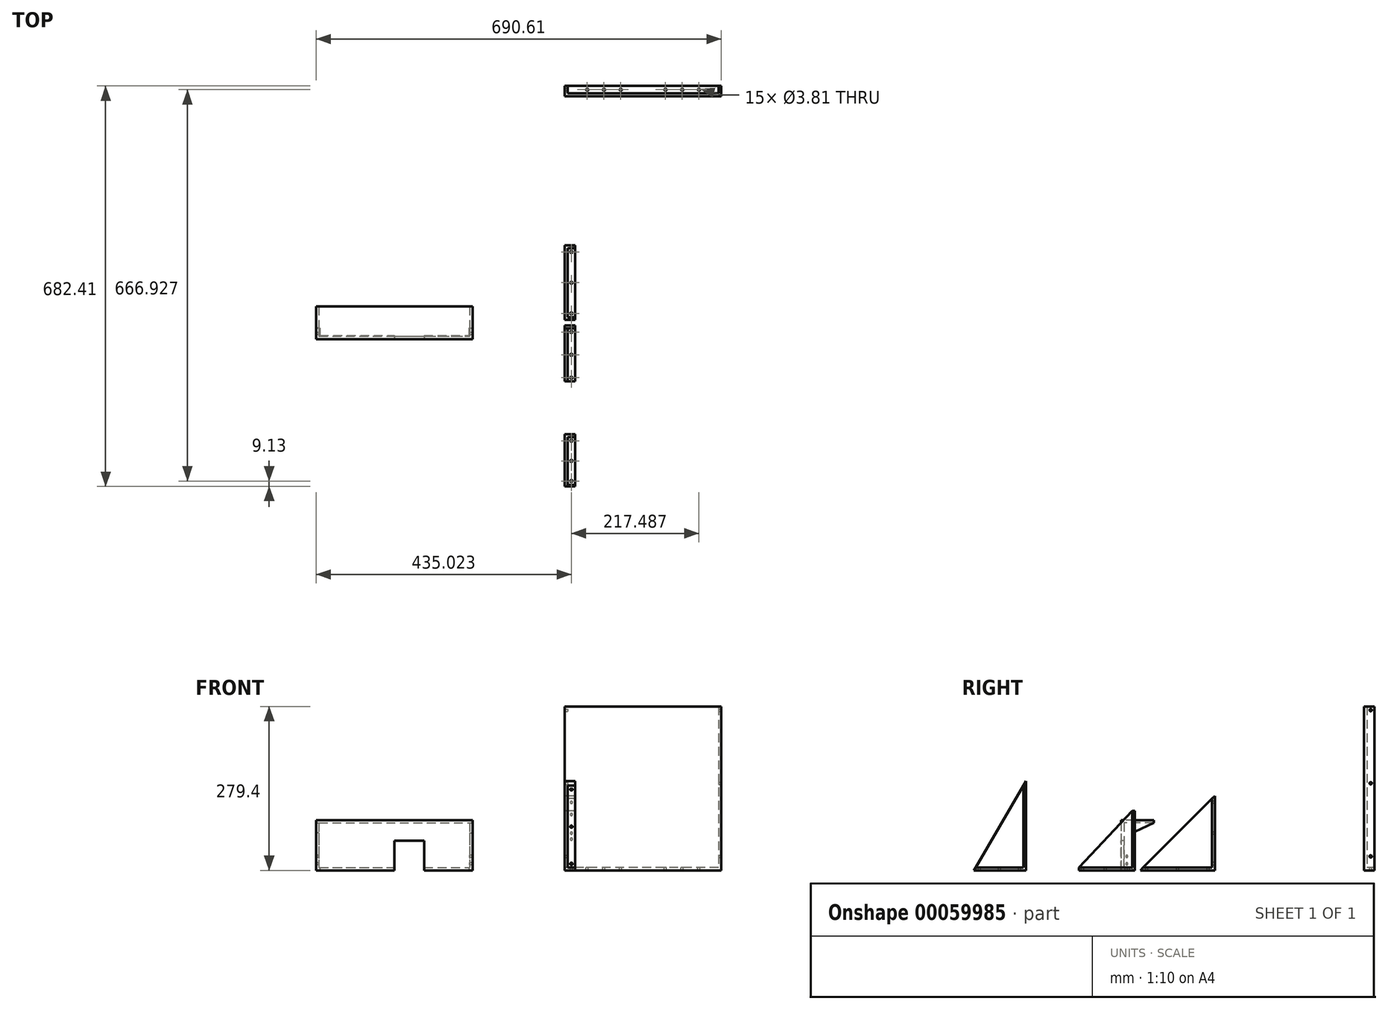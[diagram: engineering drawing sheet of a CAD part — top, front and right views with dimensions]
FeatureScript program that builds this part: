
annotation { "Feature Type Name" : "Feature", "Feature Type Description" : "" }
export const myFeature = defineFeature(function(context is Context, id is Id, definition is map)
    precondition{}
    {
        {
            var Q0;
            Q0=qCreatedBy(makeId("Right.planeOp"),FACE);
            var sketch = newSketch(context, id + "F0", { "sketchPlane" : qUnion([Q0])});
            skLineSegment(sketch, "E0", {"start": v(0, 0) * mm, "end": v(127, 127) * mm});
            skLineSegment(sketch, "E1", {"start": v(127, 127) * mm, "end": v(127, 0) * mm});
            skLineSegment(sketch, "E2", {"start": v(127, 0) * mm, "end": v(0, 0) * mm});
            skSolve(sketch);
        }
        {
            var Q0;
            Q0=makeQuery(id+"F0.imprint","IMPRINT",FACE,{"disambiguationData":[TD([[makeQuery(id+"F0.imprint","IMPRINT",EDGE,{"derivedFrom":sQuery(id+"F0.wireOp",EDGE,"E0")}),-1.0]])]});
            extrude(context, id + "F1", {"entities" : qUnion([Q0]), "depth" : 4.76 * mm});
        }
        {
            var Q0;
            Q0=makeQuery(id+"F1.opExtrude","CAP_FACE",FACE,{"disambiguationData":[OSD([sQuery(id+"F0.wireOp",EDGE,"E0"),sQuery(id+"F0.wireOp",EDGE,"E1"),sQuery(id+"F0.wireOp",EDGE,"E2")])],"isStart":false});
            var sketch = newSketch(context, id + "F2", { "sketchPlane" : qUnion([Q0])});
            skLineSegment(sketch, "E3", {"start": v(127, 4.76) * mm, "end": v(4.76, 4.76) * mm});
            skLineSegment(sketch, "E4", {"start": v(122.24, 4.76) * mm, "end": v(122.24, 122.24) * mm});
            skSolve(sketch);
        }
        {
            var Q0;
            {var subQ3=sQuery(id+"F2.wireOp",EDGE,"E4");Q0=makeQuery(id+"F2.imprint","IMPRINT",FACE,{"disambiguationData":[TD([[makeQuery(id+"F2.imprint","IMPRINT",EDGE,{"derivedFrom":subQ3}),-1.0]])]});}
            var Q1;
            {var subQ0=makeQuery(id+"F1.opExtrude","CAP_EDGE",EDGE,{"disambiguationData":[OSD([sQuery(id+"F0.wireOp",EDGE,"E2")])],"isStart":false});Q1=makeQuery(id+"F2.imprint","IMPRINT",FACE,{"disambiguationData":[TD([[makeQuery(id+"F2.imprint","IMPRINT",EDGE,{"derivedFrom":subQ0}),-1.0]])]});}
            extrude(context, id + "F3", {"entities" : qUnion([Q0, Q1]), "operationType" : NewBodyOperationType.ADD, "depth" : 12.7 * mm});
        }
        {
            var Q0;
            Q0=makeQuery(id+"F3.opExtrude","SWEPT_FACE",FACE,{"disambiguationData":[OSD([sQuery(id+"F2.wireOp",EDGE,"E3")])]});
            var sketch = newSketch(context, id + "F4", { "sketchPlane" : qUnion([Q0])});
            skCircle(sketch, "E5", {"center": v(11.11, 11.11) * mm, "radius": 1.9 * mm});
            skPoint(sketch, "E5.centerSnap0", {"position": v(11.11, 4.76) * mm});
            skCircle(sketch, "E6", {"center": v(11.11, 115.89) * mm, "radius": 1.9 * mm});
            skCircle(sketch, "E7", {"center": v(11.11, 63.5) * mm, "radius": 1.9 * mm});
            skPoint(sketch, "E7.centerSnap0", {"position": v(17.46, 63.5) * mm});
            skSolve(sketch);
        }
        {
            var Q0;
            Q0 = qSketchRegion(id + "F4", true);
            extrude(context, id + "F5", {"entities" : qUnion([Q0]), "operationType" : NewBodyOperationType.REMOVE, "endBound" : BoundingType.UP_TO_NEXT, "oppositeDirection" : true, "depth" : 25.4 * mm});
        }
        {
            var Q0;
            Q0=makeQuery(id+"F3.opExtrude","SWEPT_FACE",FACE,{"disambiguationData":[OSD([sQuery(id+"F2.wireOp",EDGE,"E4")])]});
            var sketch = newSketch(context, id + "F6", { "sketchPlane" : qUnion([Q0])});
            skCircle(sketch, "E8", {"center": v(11.11, 115.89) * mm, "radius": 1.9 * mm});
            skPoint(sketch, "E8.centerSnap0", {"position": v(11.11, 122.24) * mm});
            skCircle(sketch, "E9", {"center": v(11.11, 11.11) * mm, "radius": 2.54 * mm});
            skCircle(sketch, "E10", {"center": v(11.11, 63.5) * mm, "radius": 1.9 * mm});
            skPoint(sketch, "E10.centerSnap0", {"position": v(17.46, 63.5) * mm});
            skSolve(sketch);
        }
        {
            var Q0;
            Q0=makeQuery(id+"F6.imprint","IMPRINT",FACE,{"disambiguationData":[TD([[makeQuery(id+"F6.imprint","IMPRINT",EDGE,{"derivedFrom":sQuery(id+"F6.wireOp",EDGE,"E8")}),1.0]])]});
            var Q1;
            Q1=makeQuery(id+"F6.imprint","IMPRINT",FACE,{"disambiguationData":[TD([[makeQuery(id+"F6.imprint","IMPRINT",EDGE,{"derivedFrom":sQuery(id+"F6.wireOp",EDGE,"E9")}),1.0]])]});
            var Q2;
            Q2=makeQuery(id+"F6.imprint","IMPRINT",FACE,{"disambiguationData":[TD([[makeQuery(id+"F6.imprint","IMPRINT",EDGE,{"derivedFrom":sQuery(id+"F6.wireOp",EDGE,"E10")}),1.0]])]});
            extrude(context, id + "F7", {"entities" : qUnion([Q0, Q1, Q2]), "operationType" : NewBodyOperationType.REMOVE, "endBound" : BoundingType.UP_TO_NEXT, "oppositeDirection" : true, "depth" : 25.4 * mm});
        }
        {
            var Q0;
            Q0=qCreatedBy(makeId("Right.planeOp"),FACE);
            var sketch = newSketch(context, id + "F8", { "sketchPlane" : qUnion([Q0])});
            skLineSegment(sketch, "E11", {"start": v(-283.58, 0) * mm, "end": v(-194.68, 152.4) * mm});
            skLineSegment(sketch, "E12", {"start": v(-194.68, 152.4) * mm, "end": v(-194.68, 0) * mm});
            skLineSegment(sketch, "E13", {"start": v(-194.68, 0) * mm, "end": v(-283.58, 0) * mm});
            skSolve(sketch);
        }
        {
            var Q0;
            Q0=makeQuery(id+"F8.imprint","IMPRINT",FACE,{"disambiguationData":[TD([[makeQuery(id+"F8.imprint","IMPRINT",EDGE,{"derivedFrom":sQuery(id+"F8.wireOp",EDGE,"E11")}),-1.0]])]});
            extrude(context, id + "F9", {"entities" : qUnion([Q0]), "depth" : 4.76 * mm});
        }
        {
            var Q0;
            Q0=makeQuery(id+"F9.opExtrude","CAP_FACE",FACE,{"disambiguationData":[OSD([sQuery(id+"F8.wireOp",EDGE,"E11"),sQuery(id+"F8.wireOp",EDGE,"E12"),sQuery(id+"F8.wireOp",EDGE,"E13")])],"isStart":false});
            var sketch = newSketch(context, id + "F10", { "sketchPlane" : qUnion([Q0])});
            skLineSegment(sketch, "E14", {"start": v(-280.8, 4.76) * mm, "end": v(-194.68, 4.76) * mm});
            skLineSegment(sketch, "E15", {"start": v(-199.44, 4.76) * mm, "end": v(-199.44, 144.24) * mm});
            skSolve(sketch);
        }
        {
            var Q0;
            {var subQ3=sQuery(id+"F10.wireOp",EDGE,"E15");Q0=makeQuery(id+"F10.imprint","IMPRINT",FACE,{"disambiguationData":[TD([[makeQuery(id+"F10.imprint","IMPRINT",EDGE,{"derivedFrom":subQ3}),-1.0]])]});}
            var Q1;
            {var subQ0=makeQuery(id+"F9.opExtrude","CAP_EDGE",EDGE,{"disambiguationData":[OSD([sQuery(id+"F8.wireOp",EDGE,"E13")])],"isStart":false});Q1=makeQuery(id+"F10.imprint","IMPRINT",FACE,{"disambiguationData":[TD([[makeQuery(id+"F10.imprint","IMPRINT",EDGE,{"derivedFrom":subQ0}),-1.0]])]});}
            extrude(context, id + "F11", {"entities" : qUnion([Q0, Q1]), "operationType" : NewBodyOperationType.ADD, "depth" : 12.7 * mm});
        }
        {
            var Q0;
            Q0=makeQuery(id+"F11.opExtrude","SWEPT_FACE",FACE,{"disambiguationData":[OSD([sQuery(id+"F10.wireOp",EDGE,"E14")])]});
            var sketch = newSketch(context, id + "F12", { "sketchPlane" : qUnion([Q0])});
            skCircle(sketch, "E16", {"center": v(11.11, -274.45) * mm, "radius": 1.9 * mm});
            skPoint(sketch, "E16.centerSnap0", {"position": v(11.11, -280.8) * mm});
            skCircle(sketch, "E17", {"center": v(11.11, -205.8) * mm, "radius": 1.9 * mm});
            skPoint(sketch, "E17.centerSnap0", {"position": v(11.11, -199.44) * mm});
            skCircle(sketch, "E18", {"center": v(11.11, -240.12) * mm, "radius": 1.9 * mm});
            skPoint(sketch, "E18.centerSnap0", {"position": v(17.46, -240.12) * mm});
            skSolve(sketch);
        }
        {
            var Q0;
            Q0=makeQuery(id+"F12.imprint","IMPRINT",FACE,{"disambiguationData":[TD([[makeQuery(id+"F12.imprint","IMPRINT",EDGE,{"derivedFrom":sQuery(id+"F12.wireOp",EDGE,"E16")}),1.0]])]});
            var Q1;
            Q1=makeQuery(id+"F12.imprint","IMPRINT",FACE,{"disambiguationData":[TD([[makeQuery(id+"F12.imprint","IMPRINT",EDGE,{"derivedFrom":sQuery(id+"F12.wireOp",EDGE,"E18")}),1.0]])]});
            var Q2;
            Q2=makeQuery(id+"F12.imprint","IMPRINT",FACE,{"disambiguationData":[TD([[makeQuery(id+"F12.imprint","IMPRINT",EDGE,{"derivedFrom":sQuery(id+"F12.wireOp",EDGE,"E17")}),1.0]])]});
            extrude(context, id + "F13", {"entities" : qUnion([Q0, Q1, Q2]), "operationType" : NewBodyOperationType.REMOVE, "endBound" : BoundingType.UP_TO_NEXT, "oppositeDirection" : true, "depth" : 25.4 * mm});
        }
        {
            var Q0;
            Q0=makeQuery(id+"F11.opExtrude","SWEPT_FACE",FACE,{"disambiguationData":[OSD([sQuery(id+"F10.wireOp",EDGE,"E15")])]});
            var sketch = newSketch(context, id + "F14", { "sketchPlane" : qUnion([Q0])});
            skCircle(sketch, "E19", {"center": v(11.11, 137.89) * mm, "radius": 1.9 * mm});
            skPoint(sketch, "E19.centerSnap0", {"position": v(11.11, 144.24) * mm});
            skCircle(sketch, "E20", {"center": v(11.11, 11.11) * mm, "radius": 1.9 * mm});
            skPoint(sketch, "E20.centerSnap0", {"position": v(11.11, 4.76) * mm});
            skCircle(sketch, "E21", {"center": v(11.11, 74.5) * mm, "radius": 1.9 * mm});
            skPoint(sketch, "E21.centerSnap0", {"position": v(4.76, 74.5) * mm});
            skSolve(sketch);
        }
        {
            var Q0;
            Q0 = qSketchRegion(id + "F14", true);
            extrude(context, id + "F15", {"entities" : qUnion([Q0]), "operationType" : NewBodyOperationType.REMOVE, "endBound" : BoundingType.UP_TO_NEXT, "oppositeDirection" : true, "depth" : 25.4 * mm});
        }
        {
            var Q0;
            Q0=qCreatedBy(makeId("Right.planeOp"),FACE);
            var sketch = newSketch(context, id + "F16", { "sketchPlane" : qUnion([Q0])});
            skLineSegment(sketch, "E22", {"start": v(-104.62, 0) * mm, "end": v(-9.37, 0) * mm});
            skLineSegment(sketch, "E23", {"start": v(-9.37, 0) * mm, "end": v(-9.37, 101.6) * mm});
            skLineSegment(sketch, "E24", {"start": v(-9.37, 101.6) * mm, "end": v(-14.14, 101.6) * mm});
            skLineSegment(sketch, "E25", {"start": v(-14.14, 101.6) * mm, "end": v(-104.62, 4.76) * mm});
            skLineSegment(sketch, "E26", {"start": v(-104.62, 4.76) * mm, "end": v(-104.62, 0) * mm});
            skLineSegment(sketch, "E27", {"start": v(-104.62, 4.76) * mm, "end": v(-14.14, 4.76) * mm});
            skLineSegment(sketch, "E28", {"start": v(-14.14, 4.76) * mm, "end": v(-14.14, 101.6) * mm});
            skSolve(sketch);
        }
        {
            var Q0;
            Q0 = qSketchRegion(id + "F16", true);
            extrude(context, id + "F17", {"entities" : qUnion([Q0]), "depth" : 4.76 * mm});
        }
        {
            var Q0;
            Q0=makeQuery(id+"F17.opExtrude","CAP_FACE",FACE,{"disambiguationData":[OSD([sQuery(id+"F16.wireOp",EDGE,"E22"),sQuery(id+"F16.wireOp",EDGE,"E23"),sQuery(id+"F16.wireOp",EDGE,"E24"),sQuery(id+"F16.wireOp",EDGE,"E25"),sQuery(id+"F16.wireOp",EDGE,"E26")])],"isStart":false});
            var sketch = newSketch(context, id + "F18", { "sketchPlane" : qUnion([Q0])});
            skLineSegment(sketch, "E29", {"start": v(-14.14, 101.6) * mm, "end": v(-14.14, 4.76) * mm});
            skLineSegment(sketch, "E30", {"start": v(-14.14, 4.76) * mm, "end": v(-104.62, 4.76) * mm});
            skSolve(sketch);
        }
        {
            var Q0;
            Q0=makeQuery(id+"F18.imprint","IMPRINT",FACE,{"disambiguationData":[TD([[makeQuery(id+"F18.imprint","IMPRINT",EDGE,{"derivedFrom":sQuery(id+"F18.wireOp",EDGE,"E29")}),1.0]])]});
            extrude(context, id + "F19", {"entities" : qUnion([Q0]), "operationType" : NewBodyOperationType.ADD, "depth" : 12.7 * mm});
        }
        {
            var Q0;
            Q0=makeQuery(id+"F19.opExtrude","SWEPT_FACE",FACE,{"disambiguationData":[OSD([sQuery(id+"F18.wireOp",EDGE,"E30")])]});
            var sketch = newSketch(context, id + "F20", { "sketchPlane" : qUnion([Q0])});
            skCircle(sketch, "E31", {"center": v(11.11, -98.27) * mm, "radius": 1.9 * mm});
            skPoint(sketch, "E31.centerSnap0", {"position": v(11.11, -104.62) * mm});
            skCircle(sketch, "E32", {"center": v(11.11, -20.49) * mm, "radius": 1.9 * mm});
            skPoint(sketch, "E32.centerSnap0", {"position": v(11.11, -14.14) * mm});
            skCircle(sketch, "E33", {"center": v(11.11, -59.38) * mm, "radius": 1.9 * mm});
            skPoint(sketch, "E33.centerSnap0", {"position": v(17.46, -59.38) * mm});
            skSolve(sketch);
        }
        {
            var Q0;
            Q0 = qSketchRegion(id + "F20", true);
            extrude(context, id + "F21", {"entities" : qUnion([Q0]), "operationType" : NewBodyOperationType.REMOVE, "endBound" : BoundingType.UP_TO_NEXT, "oppositeDirection" : true, "depth" : 25.4 * mm});
        }
        {
            var Q0;
            Q0=makeQuery(id+"F19.opExtrude","SWEPT_FACE",FACE,{"disambiguationData":[OSD([sQuery(id+"F18.wireOp",EDGE,"E29")])]});
            var sketch = newSketch(context, id + "F22", { "sketchPlane" : qUnion([Q0])});
            skCircle(sketch, "E34", {"center": v(11.11, 95.25) * mm, "radius": 1.9 * mm});
            skPoint(sketch, "E34.centerSnap0", {"position": v(11.11, 101.6) * mm});
            skCircle(sketch, "E35", {"center": v(11.11, 11.11) * mm, "radius": 1.9 * mm});
            skPoint(sketch, "E35.centerSnap0", {"position": v(11.11, 4.76) * mm});
            skCircle(sketch, "E36", {"center": v(11.11, 53.18) * mm, "radius": 1.9 * mm});
            skPoint(sketch, "E36.centerSnap0", {"position": v(17.46, 53.18) * mm});
            skSolve(sketch);
        }
        {
            var Q0;
            Q0 = qSketchRegion(id + "F22", true);
            extrude(context, id + "F23", {"entities" : qUnion([Q0]), "operationType" : NewBodyOperationType.REMOVE, "endBound" : BoundingType.UP_TO_NEXT, "oppositeDirection" : true, "depth" : 25.4 * mm});
        }
        {
            var Q0;
            Q0=qCreatedBy(makeId("Top.planeOp"),FACE);
            var sketch = newSketch(context, id + "F24", { "sketchPlane" : qUnion([Q0])});
            skLineSegment(sketch, "E37.bottom", {"start": v(-423.91, -13.53) * mm, "end": v(-157.21, -13.53) * mm});
            skLineSegment(sketch, "E37.top", {"start": v(-423.91, -32.58) * mm, "end": v(-157.21, -32.58) * mm});
            skLineSegment(sketch, "E37.left", {"start": v(-423.91, -13.53) * mm, "end": v(-423.91, -32.58) * mm});
            skLineSegment(sketch, "E37.right", {"start": v(-157.21, -13.53) * mm, "end": v(-157.21, -32.58) * mm});
            skLineSegment(sketch, "E38.bottom", {"start": v(-417.56, -13.53) * mm, "end": v(-163.56, -13.53) * mm});
            skLineSegment(sketch, "E38.top", {"start": v(-417.56, -26.23) * mm, "end": v(-163.56, -26.23) * mm});
            skLineSegment(sketch, "E38.left", {"start": v(-417.56, -13.53) * mm, "end": v(-417.56, -26.23) * mm});
            skLineSegment(sketch, "E38.right", {"start": v(-163.56, -13.53) * mm, "end": v(-163.56, -26.23) * mm});
            skSolve(sketch);
        }
        {
            var Q0;
            Q0=makeQuery(id+"F24.imprint","IMPRINT",FACE,{"disambiguationData":[TD([[makeQuery(id+"F24.imprint","IMPRINT",EDGE,{"derivedFrom":sQuery(id+"F24.wireOp",EDGE,"E38.bottom")}),-1.0]])]});
            var Q1;
            Q1=makeQuery(id+"F24.imprint","IMPRINT",FACE,{"disambiguationData":[TD([[makeQuery(id+"F24.imprint","IMPRINT",EDGE,{"derivedFrom":sQuery(id+"F24.wireOp",EDGE,"E37.top")}),1.0]])]});
            extrude(context, id + "F25", {"entities" : qUnion([Q0, Q1]), "depth" : 4.76 * mm});
        }
        {
            var Q0;
            Q0=makeQuery(id+"F25.opExtrude","CAP_FACE",FACE,{"disambiguationData":[OSD([sQuery(id+"F24.wireOp",EDGE,"E37.bottom"),sQuery(id+"F24.wireOp",EDGE,"E37.top"),sQuery(id+"F24.wireOp",EDGE,"E37.left"),sQuery(id+"F24.wireOp",EDGE,"E37.right"),sQuery(id+"F24.wireOp",EDGE,"E38.bottom")])],"isStart":false});
            var sketch = newSketch(context, id + "F26", { "sketchPlane" : qUnion([Q0])});
            skLineSegment(sketch, "E39.bottom", {"start": v(-419.15, -13.53) * mm, "end": v(-161.97, -13.53) * mm});
            skLineSegment(sketch, "E39.top", {"start": v(-419.15, -27.82) * mm, "end": v(-161.97, -27.82) * mm});
            skLineSegment(sketch, "E39.left", {"start": v(-419.15, -13.53) * mm, "end": v(-419.15, -27.82) * mm});
            skLineSegment(sketch, "E39.right", {"start": v(-161.97, -13.53) * mm, "end": v(-161.97, -27.82) * mm});
            skSolve(sketch);
        }
        {
            var Q0;
            Q0=makeQuery(id+"F26.imprint","IMPRINT",FACE,{"disambiguationData":[TD([[makeQuery(id+"F26.imprint","IMPRINT",EDGE,{"derivedFrom":sQuery(id+"F26.wireOp",EDGE,"E39.top")}),-1.0]])]});
            extrude(context, id + "F27", {"entities" : qUnion([Q0]), "operationType" : NewBodyOperationType.ADD, "depth" : 76.2 * mm});
        }
        {
            var Q0;
            {var subQ0=sQuery(id+"F24.wireOp",EDGE,"E37.left");Q0=makeQuery(id+"F27.boolean.opBoolean","MERGE",FACE,{"derivedFrom":[makeQuery(id+"F25.opExtrude","SWEPT_FACE",FACE,{"disambiguationData":[OSD([subQ0])]}),makeQuery(id+"F27.opExtrude","SWEPT_FACE",FACE,{"disambiguationData":[OSD([subQ0])]})]});}
            var sketch = newSketch(context, id + "F28", { "sketchPlane" : qUnion([Q0])});
            skCircle(sketch, "E40", {"center": v(23.06, 11.11) * mm, "radius": 1.9 * mm});
            skCircle(sketch, "E41", {"center": v(23.06, 23.81) * mm, "radius": 1.9 * mm});
            skSolve(sketch);
        }
        {
            var Q0;
            Q0=makeQuery(id+"F28.imprint","IMPRINT",FACE,{"disambiguationData":[TD([[makeQuery(id+"F28.imprint","IMPRINT",EDGE,{"derivedFrom":sQuery(id+"F28.wireOp",EDGE,"E41")}),1.0]])]});
            var Q1;
            Q1=makeQuery(id+"F28.imprint","IMPRINT",FACE,{"disambiguationData":[TD([[makeQuery(id+"F28.imprint","IMPRINT",EDGE,{"derivedFrom":sQuery(id+"F28.wireOp",EDGE,"E40")}),1.0]])]});
            var Q2;
            {var subQ0=sQuery(id+"F24.wireOp",EDGE,"E37.right");Q2=makeQuery(id+"F27.boolean.opBoolean","MERGE",FACE,{"derivedFrom":[makeQuery(id+"F25.opExtrude","SWEPT_FACE",FACE,{"disambiguationData":[OSD([subQ0])]}),makeQuery(id+"F27.opExtrude","SWEPT_FACE",FACE,{"disambiguationData":[OSD([subQ0])]})]});}
            extrude(context, id + "F29", {"entities" : qUnion([Q0, Q1]), "operationType" : NewBodyOperationType.REMOVE, "endBound" : BoundingType.UP_TO_SURFACE, "oppositeDirection" : true, "endBoundEntityFace" : qUnion([Q2]), "depth" : 25.4 * mm});
        }
        {
            var Q0;
            {var subQ0=sQuery(id+"F24.wireOp",EDGE,"E37.top");Q0=makeQuery(id+"F27.boolean.opBoolean","MERGE",FACE,{"derivedFrom":[makeQuery(id+"F25.opExtrude","SWEPT_FACE",FACE,{"disambiguationData":[OSD([subQ0])]}),makeQuery(id+"F27.opExtrude","SWEPT_FACE",FACE,{"disambiguationData":[OSD([subQ0])]})]});}
            var sketch = newSketch(context, id + "F30", { "sketchPlane" : qUnion([Q0])});
            skLineSegment(sketch, "E42.bottom", {"start": v(-290.56, 0) * mm, "end": v(-239.76, 0) * mm});
            skLineSegment(sketch, "E42.top", {"start": v(-290.56, 50.8) * mm, "end": v(-239.76, 50.8) * mm});
            skLineSegment(sketch, "E42.left", {"start": v(-290.56, 0) * mm, "end": v(-290.56, 50.8) * mm});
            skLineSegment(sketch, "E42.right", {"start": v(-239.76, 0) * mm, "end": v(-239.76, 50.8) * mm});
            skLineSegment(sketch, "E43", {"start": v(-290.56, 50.8) * mm, "end": v(-423.91, 50.8) * mm, "construction": true});
            skLineSegment(sketch, "E44", {"start": v(-239.76, 50.8) * mm, "end": v(-157.21, 50.8) * mm, "construction": true});
            skSolve(sketch);
        }
        {
            var Q0;
            Q0=makeQuery(id+"F30.imprint","IMPRINT",FACE,{"disambiguationData":[TD([[makeQuery(id+"F30.imprint","IMPRINT",EDGE,{"derivedFrom":sQuery(id+"F30.wireOp",EDGE,"E42.bottom")}),1.0]])]});
            extrude(context, id + "F31", {"entities" : qUnion([Q0]), "operationType" : NewBodyOperationType.REMOVE, "endBound" : BoundingType.UP_TO_NEXT, "oppositeDirection" : true, "depth" : 25.4 * mm});
        }
        {
            var Q0;
            Q0=makeQuery(id+"F27.opExtrude","CAP_FACE",FACE,{"disambiguationData":[OSD([sQuery(id+"F24.wireOp",EDGE,"E37.bottom"),sQuery(id+"F24.wireOp",EDGE,"E37.top"),sQuery(id+"F24.wireOp",EDGE,"E37.left"),sQuery(id+"F24.wireOp",EDGE,"E37.right"),sQuery(id+"F24.wireOp",EDGE,"E38.bottom"),sQuery(id+"F26.wireOp",EDGE,"E39.top"),sQuery(id+"F26.wireOp",EDGE,"E39.left"),sQuery(id+"F26.wireOp",EDGE,"E39.right")])],"isStart":false});
            var sketch = newSketch(context, id + "F32", { "sketchPlane" : qUnion([Q0])});
            skLineSegment(sketch, "E45.bottom", {"start": v(-423.91, -32.58) * mm, "end": v(-157.21, -32.58) * mm});
            skLineSegment(sketch, "E45.top", {"start": v(-423.91, -27.82) * mm, "end": v(-157.21, -27.82) * mm});
            skLineSegment(sketch, "E45.left", {"start": v(-423.91, -32.58) * mm, "end": v(-423.91, -27.82) * mm});
            skLineSegment(sketch, "E45.right", {"start": v(-157.21, -32.58) * mm, "end": v(-157.21, -27.82) * mm});
            skSolve(sketch);
        }
        {
            var Q0;
            Q0=makeQuery(id+"F32.imprint","IMPRINT",FACE,{"disambiguationData":[TD([[makeQuery(id+"F32.imprint","IMPRINT",EDGE,{"derivedFrom":sQuery(id+"F32.wireOp",EDGE,"E45.bottom")}),1.0]])]});
            extrude(context, id + "F33", {"entities" : qUnion([Q0]), "operationType" : NewBodyOperationType.ADD, "depth" : 4.76 * mm});
        }
        {
            var Q0;
            Q0=makeQuery(id+"F33.boolean.opBoolean","MERGE",FACE,{"derivedFrom":[makeQuery(id+"F27.opExtrude","SWEPT_FACE",FACE,{"disambiguationData":[OSD([sQuery(id+"F26.wireOp",EDGE,"E39.top")])]}),makeQuery(id+"F33.opExtrude","SWEPT_FACE",FACE,{"disambiguationData":[OSD([sQuery(id+"F32.wireOp",EDGE,"E45.top")])]})]});
            var sketch = newSketch(context, id + "F34", { "sketchPlane" : qUnion([Q0])});
            skLineSegment(sketch, "E46.bottom", {"start": v(157.21, 85.73) * mm, "end": v(423.91, 85.73) * mm});
            skLineSegment(sketch, "E46.top", {"start": v(157.21, 80.96) * mm, "end": v(423.91, 80.96) * mm});
            skLineSegment(sketch, "E46.left", {"start": v(157.21, 85.73) * mm, "end": v(157.21, 80.96) * mm});
            skLineSegment(sketch, "E46.right", {"start": v(423.91, 85.73) * mm, "end": v(423.91, 80.96) * mm});
            skSolve(sketch);
        }
        {
            var Q0;
            Q0=makeQuery(id+"F34.imprint","IMPRINT",FACE,{"disambiguationData":[TD([[makeQuery(id+"F34.imprint","IMPRINT",EDGE,{"derivedFrom":sQuery(id+"F34.wireOp",EDGE,"E46.bottom")}),1.0]])]});
            extrude(context, id + "F35", {"entities" : qUnion([Q0]), "operationType" : NewBodyOperationType.ADD, "depth" : 50.8 * mm});
        }
        {
            var Q0;
            {var subQ0=sQuery(id+"F24.wireOp",EDGE,"E37.left");Q0=makeQuery(id+"F35.boolean.opBoolean","MERGE",FACE,{"derivedFrom":[makeQuery(id+"F33.boolean.opBoolean","MERGE",FACE,{"derivedFrom":[makeQuery(id+"F27.boolean.opBoolean","MERGE",FACE,{"derivedFrom":[makeQuery(id+"F25.opExtrude","SWEPT_FACE",FACE,{"disambiguationData":[OSD([subQ0])]}),makeQuery(id+"F27.opExtrude","SWEPT_FACE",FACE,{"disambiguationData":[OSD([subQ0])]})]}),makeQuery(id+"F33.opExtrude","SWEPT_FACE",FACE,{"disambiguationData":[OSD([sQuery(id+"F32.wireOp",EDGE,"E45.left")])]})]}),makeQuery(id+"F35.opExtrude","SWEPT_FACE",FACE,{"disambiguationData":[OSD([sQuery(id+"F34.wireOp",EDGE,"E46.right")])]})]});}
            var sketch = newSketch(context, id + "F36", { "sketchPlane" : qUnion([Q0])});
            skLineSegment(sketch, "E47", {"start": v(-22.98, 80.96) * mm, "end": v(13.53, 63.94) * mm});
            skSolve(sketch);
        }
        {
            var Q0;
            {var subQ0=sQuery(id+"F36.wireOp",EDGE,"E47");Q0=makeQuery(id+"F36.imprint","IMPRINT",FACE,{"disambiguationData":[TD([[makeQuery(id+"F36.imprint","IMPRINT",EDGE,{"derivedFrom":subQ0}),1.0]])]});}
            extrude(context, id + "F37", {"entities" : qUnion([Q0]), "operationType" : NewBodyOperationType.ADD, "oppositeDirection" : true, "depth" : 4.76 * mm});
        }
        {
            var Q0;
            {var subQ0=sQuery(id+"F24.wireOp",EDGE,"E37.right");Q0=makeQuery(id+"F35.boolean.opBoolean","MERGE",FACE,{"derivedFrom":[makeQuery(id+"F33.boolean.opBoolean","MERGE",FACE,{"derivedFrom":[makeQuery(id+"F27.boolean.opBoolean","MERGE",FACE,{"derivedFrom":[makeQuery(id+"F25.opExtrude","SWEPT_FACE",FACE,{"disambiguationData":[OSD([subQ0])]}),makeQuery(id+"F27.opExtrude","SWEPT_FACE",FACE,{"disambiguationData":[OSD([subQ0])]})]}),makeQuery(id+"F33.opExtrude","SWEPT_FACE",FACE,{"disambiguationData":[OSD([sQuery(id+"F32.wireOp",EDGE,"E45.right")])]})]}),makeQuery(id+"F35.opExtrude","SWEPT_FACE",FACE,{"disambiguationData":[OSD([sQuery(id+"F34.wireOp",EDGE,"E46.left")])]})]});}
            var sketch = newSketch(context, id + "F38", { "sketchPlane" : qUnion([Q0])});
            skLineSegment(sketch, "E48", {"start": v(22.98, 80.96) * mm, "end": v(-13.53, 63.94) * mm});
            skSolve(sketch);
        }
        {
            var Q0;
            {var subQ0=sQuery(id+"F38.wireOp",EDGE,"E48");Q0=makeQuery(id+"F38.imprint","IMPRINT",FACE,{"disambiguationData":[TD([[makeQuery(id+"F38.imprint","IMPRINT",EDGE,{"derivedFrom":subQ0}),-1.0]])]});}
            extrude(context, id + "F39", {"entities" : qUnion([Q0]), "operationType" : NewBodyOperationType.ADD, "oppositeDirection" : true, "depth" : 4.76 * mm});
        }
        {
            var Q0;
            Q0=qCreatedBy(makeId("Right.planeOp"),FACE);
            var sketch = newSketch(context, id + "F40", { "sketchPlane" : qUnion([Q0])});
            skLineSegment(sketch, "E49.bottom", {"start": v(381.37, 0) * mm, "end": v(386.13, 0) * mm});
            skLineSegment(sketch, "E49.top", {"start": v(381.37, 279.4) * mm, "end": v(386.13, 279.4) * mm});
            skLineSegment(sketch, "E49.left", {"start": v(381.37, 0) * mm, "end": v(381.37, 279.4) * mm});
            skLineSegment(sketch, "E49.right", {"start": v(386.13, 0) * mm, "end": v(386.13, 279.4) * mm});
            skSolve(sketch);
        }
        {
            var Q0;
            Q0=makeQuery(id+"F40.imprint","IMPRINT",FACE,{"disambiguationData":[TD([[makeQuery(id+"F40.imprint","IMPRINT",EDGE,{"derivedFrom":sQuery(id+"F40.wireOp",EDGE,"E49.bottom")}),1.0]])]});
            extrude(context, id + "F41", {"entities" : qUnion([Q0]), "depth" : 266.7 * mm});
        }
        {
            var Q0;
            Q0=makeQuery(id+"F41.opExtrude","SWEPT_FACE",FACE,{"disambiguationData":[OSD([sQuery(id+"F40.wireOp",EDGE,"E49.right")])]});
            var sketch = newSketch(context, id + "F42", { "sketchPlane" : qUnion([Q0])});
            skLineSegment(sketch, "E50", {"start": v(-133.35, 279.4) * mm, "end": v(-133.35, 0) * mm, "construction": true});
            skLineSegment(sketch, "E51.bottom", {"start": v(-266.7, 279.4) * mm, "end": v(-261.94, 279.4) * mm});
            skLineSegment(sketch, "E51.top", {"start": v(-266.7, 0) * mm, "end": v(-261.94, 0) * mm});
            skLineSegment(sketch, "E51.left", {"start": v(-266.7, 279.4) * mm, "end": v(-266.7, 0) * mm});
            skLineSegment(sketch, "E51.right", {"start": v(-261.94, 279.4) * mm, "end": v(-261.94, 0) * mm});
            skLineSegment(sketch, "E52.bottom", {"start": v(-261.94, 0) * mm, "end": v(-133.35, 0) * mm});
            skLineSegment(sketch, "E52.top", {"start": v(-261.94, 4.76) * mm, "end": v(-133.35, 4.76) * mm});
            skLineSegment(sketch, "E52.left", {"start": v(-261.94, 0) * mm, "end": v(-261.94, 4.76) * mm});
            skLineSegment(sketch, "E52.right", {"start": v(-133.35, 0) * mm, "end": v(-133.35, 4.76) * mm});
            skLineSegment(sketch, "E53.MirrorCS", {"start": v(-4.76, 279.4) * mm, "end": v(-4.76, 0) * mm});
            skLineSegment(sketch, "E54.MirrorCS", {"start": v(-4.76, 4.76) * mm, "end": v(-133.35, 4.76) * mm});
            skSolve(sketch);
        }
        {
            var Q0;
            Q0 = qSketchRegion(id + "F42", true);
            var Q1;
            {var subQ0=sQuery(id+"F42.wireOp",EDGE,"E52.right");Q1=makeQuery(id+"F42.imprint","IMPRINT",FACE,{"disambiguationData":[TD([[makeQuery(id+"F42.imprint","IMPRINT",EDGE,{"derivedFrom":subQ0}),-1.0]])]});}
            var Q2;
            {var subQ0=sQuery(id+"F40.wireOp",EDGE,"E49.right");var subQ1=makeQuery(id+"F41.opExtrude","CAP_EDGE",EDGE,{"disambiguationData":[OSD([subQ0])],"isStart":true});Q2=makeQuery(id+"F42.imprint","IMPRINT",FACE,{"disambiguationData":[TD([[makeQuery(id+"F42.imprint","IMPRINT",EDGE,{"derivedFrom":subQ1}),1.0]])]});}
            extrude(context, id + "F43", {"entities" : qUnion([Q0, Q1, Q2]), "operationType" : NewBodyOperationType.ADD, "depth" : 12.7 * mm});
        }
        {
            var Q0;
            Q0=makeQuery(id+"F43.boolean.opBoolean","MERGE",FACE,{"derivedFrom":[makeQuery(id+"F41.opExtrude","CAP_FACE",FACE,{"disambiguationData":[OSD([sQuery(id+"F40.wireOp",EDGE,"E49.bottom"),sQuery(id+"F40.wireOp",EDGE,"E49.top"),sQuery(id+"F40.wireOp",EDGE,"E49.left"),sQuery(id+"F40.wireOp",EDGE,"E49.right")])],"isStart":false}),makeQuery(id+"F43.opExtrude","SWEPT_FACE",FACE,{"disambiguationData":[OSD([sQuery(id+"F42.wireOp",EDGE,"E51.left")])]})]});
            var sketch = newSketch(context, id + "F44", { "sketchPlane" : qUnion([Q0])});
            skCircle(sketch, "E55", {"center": v(392.48, 273.05) * mm, "radius": 1.9 * mm});
            skCircle(sketch, "E56", {"center": v(392.48, 148.43) * mm, "radius": 1.9 * mm});
            skCircle(sketch, "E57", {"center": v(392.48, 23.81) * mm, "radius": 1.9 * mm});
            skLineSegment(sketch, "E58", {"start": v(392.48, 23.81) * mm, "end": v(392.48, 148.43) * mm, "construction": true});
            skLineSegment(sketch, "E59", {"start": v(392.48, 148.43) * mm, "end": v(392.48, 273.05) * mm, "construction": true});
            skSolve(sketch);
        }
        {
            var Q0;
            Q0 = qSketchRegion(id + "F44", true);
            var Q1;
            {var subQ0=sQuery(id+"F40.wireOp",EDGE,"E49.right");Q1=makeQuery(id+"F43.boolean.opBoolean","MERGE",FACE,{"derivedFrom":[makeQuery(id+"F41.opExtrude","CAP_FACE",FACE,{"disambiguationData":[OSD([sQuery(id+"F40.wireOp",EDGE,"E49.bottom"),sQuery(id+"F40.wireOp",EDGE,"E49.top"),sQuery(id+"F40.wireOp",EDGE,"E49.left"),subQ0])],"isStart":true}),makeQuery(id+"F43.opExtrude","SWEPT_FACE",FACE,{"disambiguationData":[OSD([subQ0])]})]});}
            extrude(context, id + "F45", {"entities" : qUnion([Q0]), "operationType" : NewBodyOperationType.REMOVE, "endBound" : BoundingType.UP_TO_SURFACE, "oppositeDirection" : true, "endBoundEntityFace" : qUnion([Q1]), "depth" : 25.4 * mm});
        }
        {
            var Q0;
            Q0=makeQuery(id+"F43.opExtrude","SWEPT_FACE",FACE,{"disambiguationData":[OSD([sQuery(id+"F42.wireOp",EDGE,"E52.top"),sQuery(id+"F42.wireOp",EDGE,"E54.MirrorCS")])]});
            var sketch = newSketch(context, id + "F46", { "sketchPlane" : qUnion([Q0])});
            skCircle(sketch, "E60", {"center": v(38.1, 392.48) * mm, "radius": 1.9 * mm});
            skPoint(sketch, "E60.centerSnap0", {"position": v(4.76, 392.48) * mm});
            skCircle(sketch, "E61", {"center": v(66.68, 392.48) * mm, "radius": 1.9 * mm});
            skCircle(sketch, "E62", {"center": v(95.25, 392.48) * mm, "radius": 1.9 * mm});
            skLineSegment(sketch, "E63", {"start": v(133.35, 398.83) * mm, "end": v(133.35, 386.13) * mm, "construction": true});
            skLineSegment(sketch, "E64", {"start": v(38.1, 392.48) * mm, "end": v(95.25, 392.48) * mm, "construction": true});
            skCircle(sketch, "E65.MirrorC", {"center": v(171.45, 392.48) * mm, "radius": 1.9 * mm});
            skLineSegment(sketch, "E66.MirrorCS", {"start": v(228.6, 392.48) * mm, "end": v(171.45, 392.48) * mm, "construction": true});
            skCircle(sketch, "E67.MirrorC", {"center": v(228.6, 392.48) * mm, "radius": 1.9 * mm});
            skCircle(sketch, "E68.MirrorC", {"center": v(200.03, 392.48) * mm, "radius": 1.9 * mm});
            skSolve(sketch);
        }
        {
            var Q0;
            Q0 = qSketchRegion(id + "F46", true);
            extrude(context, id + "F47", {"entities" : qUnion([Q0]), "operationType" : NewBodyOperationType.REMOVE, "endBound" : BoundingType.UP_TO_NEXT, "oppositeDirection" : true, "depth" : 25.4 * mm});
        }
    });
